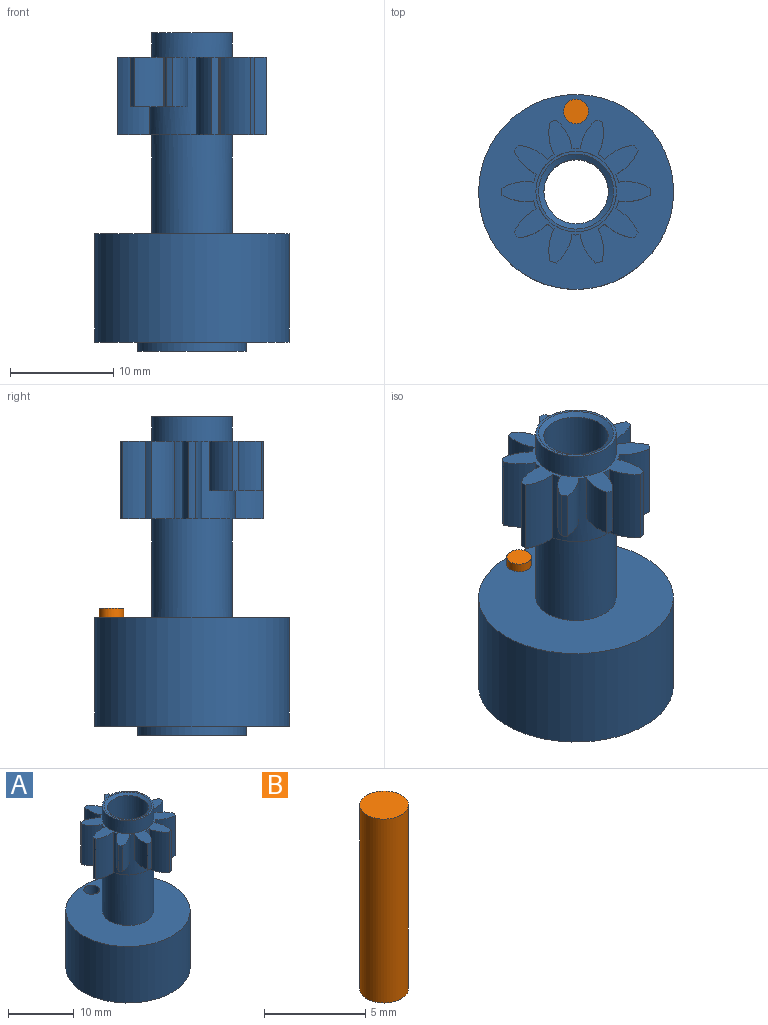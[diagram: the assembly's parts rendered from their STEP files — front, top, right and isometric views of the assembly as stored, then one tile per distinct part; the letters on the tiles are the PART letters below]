
ASSEMBLY  parts=2 mates=1
PART A: 54 faces, bbox 18.9x18.9x30.9 mm
  f0: plane 14.4x13.88mm, normal (0,0,-1), area 46.7mm2, adj f1,f2,f3,f10,f11,f12,f13,f14
  f1: cylinder r=4.5mm len=7.5mm, axis (0,0,-1), area 24.1mm2, adj f0,f2,f38,f39
  f2: cylinder r=7.2mm len=7.5mm, axis (0,0,-1), area 4.8mm2, adj f0,f1,f3,f39
  f3: cylinder r=4.5mm len=7.5mm, axis (0,0,-1), area 24.1mm2, adj f0,f2,f10,f39
  f4: cylinder r=4.5mm len=4.8mm, axis (0,0,-1), area 15.4mm2, adj f5,f10,f39,f41
  f5: cylinder r=7.2mm len=4.8mm, axis (0,0,-1), area 3.1mm2, adj f4,f6,f39,f41
  f6: cylinder r=4.5mm len=4.8mm, axis (0,0,-1), area 15.4mm2, adj f5,f10,f39,f41
  f7: cylinder r=4.5mm len=4.8mm, axis (0,0,-1), area 15.4mm2, adj f8,f10,f39,f40
  f8: cylinder r=7.2mm len=4.8mm, axis (0,0,-1), area 3.1mm2, adj f7,f9,f39,f40
  f9: cylinder r=4.5mm len=4.8mm, axis (0,0,-1), area 15.4mm2, adj f8,f10,f39,f40
  f10: cylinder r=4.2mm len=7.5mm, axis (0,0,-1), area 28mm2, adj f0,f3,f4,f6,f7,f9,f11,f39
  f11: cylinder r=4.5mm len=7.5mm, axis (0,0,-1), area 24.1mm2, adj f0,f10,f12,f39
  f12: cylinder r=7.2mm len=7.5mm, axis (0,0,-1), area 4.8mm2, adj f0,f11,f13,f39
  f13: cylinder r=4.5mm len=7.5mm, axis (0,0,-1), area 24.1mm2, adj f0,f12,f14,f39
  f14: cylinder r=4.2mm len=7.5mm, axis (0,0,-1), area 6mm2, adj f0,f13,f15,f39
  f15: cylinder r=4.5mm len=7.5mm, axis (0,0,-1), area 24.1mm2, adj f0,f14,f16,f39
  f16: cylinder r=7.2mm len=7.5mm, axis (0,0,-1), area 4.8mm2, adj f0,f15,f17,f39
  f17: cylinder r=4.5mm len=7.5mm, axis (0,0,-1), area 24.1mm2, adj f0,f16,f18,f39
  f18: cylinder r=4.2mm len=7.5mm, axis (0,0,-1), area 6mm2, adj f0,f17,f19,f39
  f19: cylinder r=4.5mm len=7.5mm, axis (0,0,-1), area 24.1mm2, adj f0,f18,f20,f39
  f20: cylinder r=7.2mm len=7.5mm, axis (0,0,-1), area 4.8mm2, adj f0,f19,f21,f39
  f21: cylinder r=4.5mm len=7.5mm, axis (0,0,-1), area 24.1mm2, adj f0,f20,f22,f39
  f22: cylinder r=4.2mm len=7.5mm, axis (0,0,-1), area 6mm2, adj f0,f21,f23,f39
  f23: cylinder r=4.5mm len=7.5mm, axis (0,0,-1), area 24.1mm2, adj f0,f22,f24,f39
  f24: cylinder r=7.2mm len=7.5mm, axis (0,0,-1), area 4.8mm2, adj f0,f23,f25,f39
  f25: cylinder r=4.5mm len=7.5mm, axis (0,0,-1), area 24.1mm2, adj f0,f24,f26,f39
  f26: cylinder r=4.2mm len=7.5mm, axis (0,0,-1), area 6mm2, adj f0,f25,f27,f39
  f27: cylinder r=4.5mm len=7.5mm, axis (0,0,-1), area 24.1mm2, adj f0,f26,f28,f39
  f28: cylinder r=7.2mm len=7.5mm, axis (0,0,-1), area 4.8mm2, adj f0,f27,f29,f39
  f29: cylinder r=4.5mm len=7.5mm, axis (0,0,-1), area 24.1mm2, adj f0,f28,f30,f39
  f30: cylinder r=4.2mm len=7.5mm, axis (0,0,-1), area 6mm2, adj f0,f29,f31,f39
  f31: cylinder r=4.5mm len=7.5mm, axis (0,0,-1), area 24.1mm2, adj f0,f30,f32,f39
  f32: cylinder r=7.2mm len=7.5mm, axis (0,0,-1), area 4.8mm2, adj f0,f31,f33,f39
  f33: cylinder r=4.5mm len=7.5mm, axis (0,0,-1), area 24.1mm2, adj f0,f32,f34,f39
  f34: cylinder r=4.2mm len=7.5mm, axis (0,0,-1), area 6mm2, adj f0,f33,f35,f39
  f35: cylinder r=4.5mm len=7.5mm, axis (0,0,-1), area 24.1mm2, adj f0,f34,f36,f39
  f36: cylinder r=7.2mm len=7.5mm, axis (0,0,-1), area 4.8mm2, adj f0,f35,f37,f39
  f37: cylinder r=4.5mm len=7.5mm, axis (0,0,-1), area 24.1mm2, adj f0,f36,f38,f39
  f38: cylinder r=4.2mm len=7.5mm, axis (0,0,-1), area 6mm2, adj f0,f1,f37,f39
  f39: plane 14.4x13.88mm, normal (0,0,1), area 56.4mm2, adj f1,f2,f3,f4,f5,f6,f7,f8
  f40: plane 3.32x2.24mm, normal (0,0,-1), area 4.9mm2, adj f7,f8,f9,f10
  f41: plane 3.22x2.81mm, normal (0,0,-1), area 4.9mm2, adj f4,f5,f6,f10
  f42: cylinder r=3.9mm len=9.6mm, axis (0,0,-1), area 235.2mm2, adj f0,f48
  f43: cone r=3.12mm half-angle=30deg, axis (0,0,-1), area 49.7mm2, adj f44,f51
  f44: plane 10.5x10.5mm, normal (0,0,-1), area 31.2mm2, adj f43,f45
  f45: cylinder r=5.25mm len=10.5mm, axis (0,0,-1), area 29.7mm2, adj f44,f46
  f46: plane 18.9x18.9mm, normal (0,0,-1), area 189.4mm2, adj f45,f47,f52
  f47: cylinder r=9.45mm len=18.9mm, axis (0,0,-1), area 623.4mm2, adj f46,f48
  f48: plane 18.9x18.9mm, normal (0,0,1), area 228.2mm2, adj f42,f47,f52
  f49: cylinder r=3.9mm len=7.8mm, axis (0,0,-1), area 58.8mm2, adj f39,f50
  f50: plane 7.8x7.8mm, normal (0,0,1), area 6.2mm2, adj f49,f53
  f51: cylinder r=3.12mm len=28.73mm, axis (0,0,-1), area 563.2mm2, adj f43,f53
  f52: cylinder r=1.2mm len=10.5mm, axis (0,0,1), area 79.2mm2, adj f46,f48
  f53: cone r=3.64mm half-angle=60deg, axis (0,0,1), area 12.7mm2, adj f50,f51
PART B: 3 faces, bbox 2.4x2.4x11.1 mm
  f0: cylinder r=1.2mm len=11.1mm, axis (0,0,-1), area 83.7mm2, adj f1,f2
  f1: plane 2.4x2.4mm, normal (0,0,1), area 4.5mm2, adj f0
  f2: plane 2.4x2.4mm, normal (0,0,-1), area 4.5mm2, adj f0
PLACE A t=(0,-5.2,-7.6)mm
PLACE B t=(0,2.6,-6.4)mm
MATE fastened B.f0 <-> A.f52  axis (0,0,1) through (0,2.6,4.7)mm
